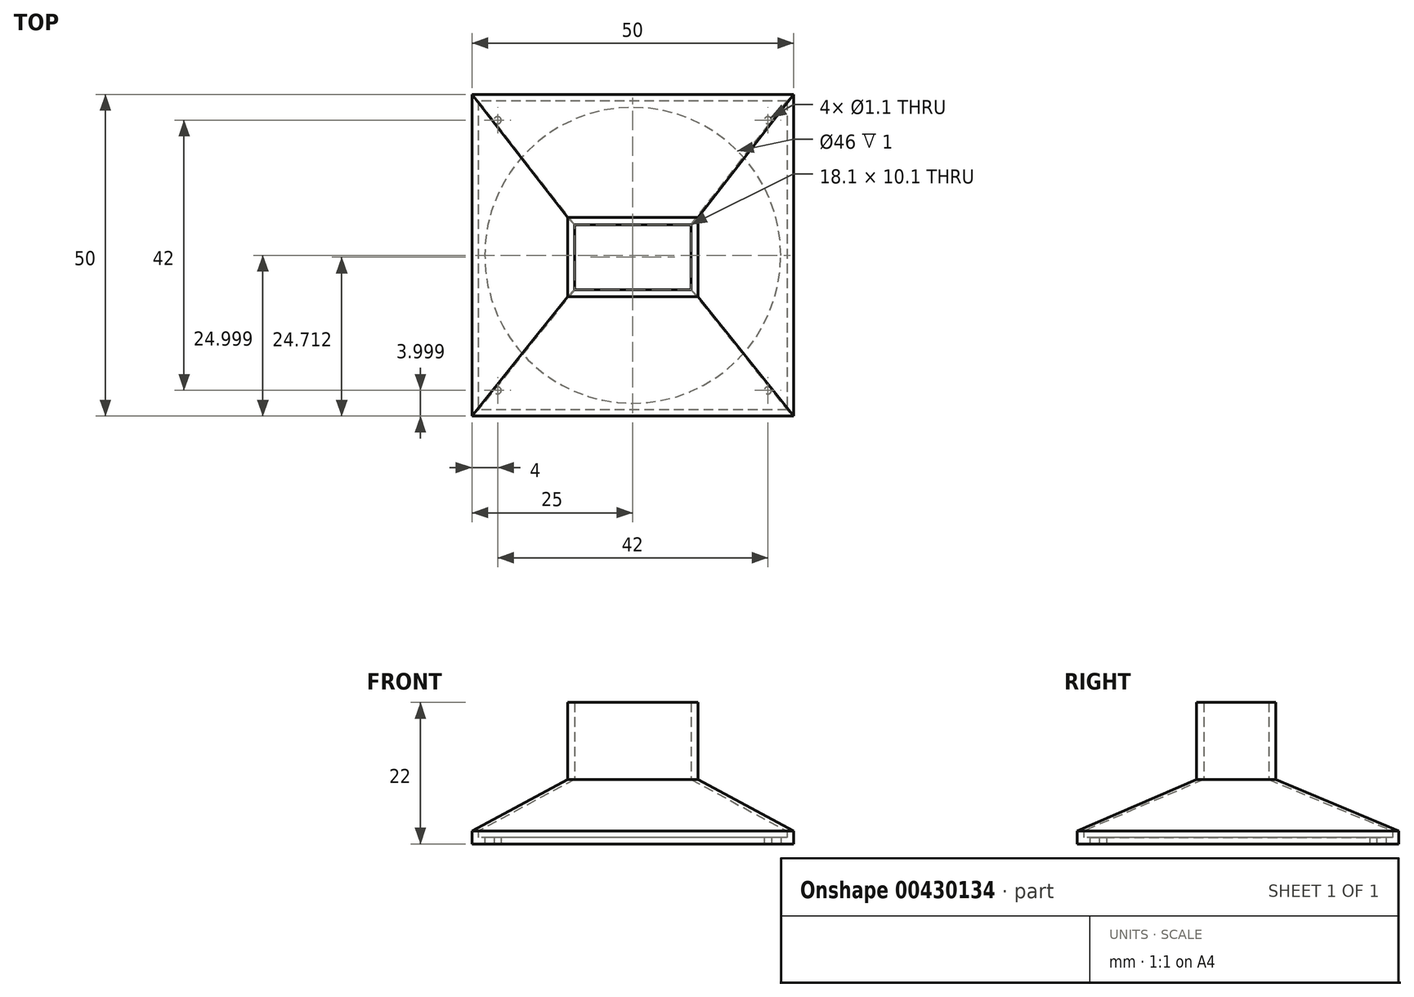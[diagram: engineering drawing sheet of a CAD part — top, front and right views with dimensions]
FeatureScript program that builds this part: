
annotation { "Feature Type Name" : "Feature", "Feature Type Description" : "" }
export const myFeature = defineFeature(function(context is Context, id is Id, definition is map)
    precondition{}
    {
        {
            var Q0;
            Q0=qCreatedBy(makeId("Top.planeOp"),FACE);
            var sketch = newSketch(context, id + "F0", { "sketchPlane" : qUnion([Q0])});
            skPoint(sketch, "E0.middle", {"position": v(0, -0.35) * mm});
            skLineSegment(sketch, "E1", {"start": v(0, 67.46) * mm, "end": v(0, -54.12) * mm, "construction": true});
            skCircle(sketch, "E2", {"center": v(0, -0.35) * mm, "radius": 23 * mm});
            skLineSegment(sketch, "E3.bottom", {"start": v(25, 24.65) * mm, "end": v(-25, 24.65) * mm});
            skLineSegment(sketch, "E3.top", {"start": v(25, -25.35) * mm, "end": v(-25, -25.35) * mm});
            skLineSegment(sketch, "E3.left", {"start": v(25, 24.65) * mm, "end": v(25, -25.35) * mm});
            skLineSegment(sketch, "E3.right", {"start": v(-25, 24.65) * mm, "end": v(-25, -25.35) * mm});
            skCircle(sketch, "E4", {"center": v(21, 20.65) * mm, "radius": 0.55 * mm});
            skCircle(sketch, "E5.MirrorC", {"center": v(-21, 20.65) * mm, "radius": 0.55 * mm});
            skCircle(sketch, "E6.MirrorC", {"center": v(-21, -21.35) * mm, "radius": 0.55 * mm});
            skCircle(sketch, "E7.MirrorC", {"center": v(21, -21.35) * mm, "radius": 0.55 * mm});
            skLineSegment(sketch, "E8.0", {"start": v(24, 23.65) * mm, "end": v(24, -24.35) * mm});
            skLineSegment(sketch, "E8.1", {"start": v(24, 23.65) * mm, "end": v(-24, 23.65) * mm});
            skLineSegment(sketch, "E8.2", {"start": v(-24, 23.65) * mm, "end": v(-24, -24.35) * mm});
            skLineSegment(sketch, "E8.3", {"start": v(24, -24.35) * mm, "end": v(-24, -24.35) * mm});
            skPoint(sketch, "E0.right.end.orphan", {"position": v(-9.05, -5.4) * mm});
            skPoint(sketch, "E9.orphan", {"position": v(-9.05, 4.7) * mm});
            skPoint(sketch, "E0.left.end.orphan", {"position": v(9.05, -5.4) * mm});
            skPoint(sketch, "E0.left.start.orphan", {"position": v(9.05, 4.7) * mm});
            skSolve(sketch);
        }
        {
            var Q0;
            Q0 = qSketchRegion(id + "F0", true);
            extrude(context, id + "F1", {"entities" : qUnion([Q0]), "depth" : 2 * mm});
        }
        {
            var Q0;
            Q0=makeQuery(id+"F0.imprint","IMPRINT",FACE,{"disambiguationData":[TD([[makeQuery(id+"F0.imprint","IMPRINT",EDGE,{"derivedFrom":sQuery(id+"F0.wireOp",EDGE,"E2")}),-1.0]])]});
            extrude(context, id + "F2", {"entities" : qUnion([Q0]), "operationType" : NewBodyOperationType.ADD, "depth" : 1 * mm});
        }
        {
            var Q0;
            Q0=qCreatedBy(makeId("Top.planeOp"),FACE);
            cPlane(context, id + "F3", {"entities" : qUnion([Q0]), "cplaneType" : CPlaneType.OFFSET, "offset" : 10 * mm, "width" : 150 * mm, "height" : 150 * mm});
        }
        {
            var Q0;
            Q0=qCreatedBy(id+"F3.planeOp",FACE);
            var sketch = newSketch(context, id + "F4", { "sketchPlane" : qUnion([Q0])});
            skLineSegment(sketch, "E10.bottom", {"start": v(9.05, 4.41) * mm, "end": v(-9.05, 4.41) * mm});
            skLineSegment(sketch, "E10.top", {"start": v(9.05, -5.69) * mm, "end": v(-9.05, -5.69) * mm});
            skLineSegment(sketch, "E10.left", {"start": v(9.05, 4.41) * mm, "end": v(9.05, -5.69) * mm});
            skLineSegment(sketch, "E10.right", {"start": v(-9.05, 4.41) * mm, "end": v(-9.05, -5.69) * mm});
            skPoint(sketch, "E10.middle", {"position": v(0, -0.64) * mm});
            skLineSegment(sketch, "E11", {"start": v(0, 67.17) * mm, "end": v(0, -54.41) * mm, "construction": true});
            skLineSegment(sketch, "E12.0", {"start": v(-10.15, 5.51) * mm, "end": v(-10.15, -6.79) * mm});
            skLineSegment(sketch, "E12.1", {"start": v(10.15, 5.51) * mm, "end": v(-10.15, 5.51) * mm});
            skLineSegment(sketch, "E12.2", {"start": v(10.15, 5.51) * mm, "end": v(10.15, -6.79) * mm});
            skLineSegment(sketch, "E12.3", {"start": v(10.15, -6.79) * mm, "end": v(-10.15, -6.79) * mm});
            skLineSegment(sketch, "E13", {"start": v(10.15, 5.51) * mm, "end": v(9.05, 4.41) * mm});
            skLineSegment(sketch, "E14", {"start": v(-9.05, 4.41) * mm, "end": v(-10.15, 5.51) * mm});
            skLineSegment(sketch, "E15", {"start": v(10.15, -6.79) * mm, "end": v(9.05, -5.69) * mm});
            skLineSegment(sketch, "E16", {"start": v(-10.15, -6.79) * mm, "end": v(-9.05, -5.69) * mm});
            skSolve(sketch);
        }
        {
            var Q0;
            Q0 = qSketchRegion(id + "F4", true);
            extrude(context, id + "F5", {"entities" : qUnion([Q0]), "depth" : 12 * mm});
        }
        {
            var Q0;
            Q0=makeQuery(id+"F1.opExtrude","CAP_FACE",FACE,{"disambiguationData":[OSD([sQuery(id+"F0.wireOp",EDGE,"E3.bottom"),sQuery(id+"F0.wireOp",EDGE,"E3.top"),sQuery(id+"F0.wireOp",EDGE,"E3.left"),sQuery(id+"F0.wireOp",EDGE,"E3.right"),sQuery(id+"F0.wireOp",EDGE,"E8.0"),sQuery(id+"F0.wireOp",EDGE,"E8.1"),sQuery(id+"F0.wireOp",EDGE,"E8.2"),sQuery(id+"F0.wireOp",EDGE,"E8.3")])],"isStart":false});
            var sketch = newSketch(context, id + "F6", { "sketchPlane" : qUnion([Q0])});
            skLineSegment(sketch, "E17", {"start": v(-24, -24.35) * mm, "end": v(-25, -25.35) * mm});
            skLineSegment(sketch, "E18", {"start": v(-24, 23.65) * mm, "end": v(-25, 24.65) * mm});
            skLineSegment(sketch, "E19", {"start": v(24, 23.65) * mm, "end": v(25, 24.65) * mm});
            skLineSegment(sketch, "E20", {"start": v(25, -25.35) * mm, "end": v(24, -24.35) * mm});
            skSolve(sketch);
        }
        {
            var Q0;
            Q0=makeQuery(id+"F4.imprint","IMPRINT",FACE,{"disambiguationData":[TD([[makeQuery(id+"F4.imprint","IMPRINT",EDGE,{"derivedFrom":sQuery(id+"F4.wireOp",EDGE,"E10.bottom")}),-1.0]])]});
            var Q1;
            Q1=makeQuery(id+"F6.imprint","IMPRINT",FACE,{"disambiguationData":[TD([[makeQuery(id+"F6.imprint","IMPRINT",EDGE,{"derivedFrom":sQuery(id+"F6.wireOp",EDGE,"E18")}),-1.0]])]});
            loft(context, id + "F7", {"sheetProfilesArray" : [{ "sheetProfileEntities" : qUnion([Q0]) }, { "sheetProfileEntities" : qUnion([Q1]) }]});
        }
        {
            var Q0;
            Q0=makeQuery(id+"F6.imprint","IMPRINT",FACE,{"disambiguationData":[TD([[makeQuery(id+"F6.imprint","IMPRINT",EDGE,{"derivedFrom":sQuery(id+"F6.wireOp",EDGE,"E17")}),1.0]])]});
            var Q1;
            Q1=makeQuery(id+"F4.imprint","IMPRINT",FACE,{"disambiguationData":[TD([[makeQuery(id+"F4.imprint","IMPRINT",EDGE,{"derivedFrom":sQuery(id+"F4.wireOp",EDGE,"E10.top")}),1.0]])]});
            loft(context, id + "F8", {"sheetProfilesArray" : [{ "sheetProfileEntities" : qUnion([Q0]) }, { "sheetProfileEntities" : qUnion([Q1]) }]});
        }
        {
            var Q0;
            Q0=makeQuery(id+"F4.imprint","IMPRINT",FACE,{"disambiguationData":[TD([[makeQuery(id+"F4.imprint","IMPRINT",EDGE,{"derivedFrom":sQuery(id+"F4.wireOp",EDGE,"E10.left")}),1.0]])]});
            var Q1;
            Q1=makeQuery(id+"F6.imprint","IMPRINT",FACE,{"disambiguationData":[TD([[makeQuery(id+"F6.imprint","IMPRINT",EDGE,{"derivedFrom":sQuery(id+"F6.wireOp",EDGE,"E19")}),-1.0]])]});
            loft(context, id + "F9", {"sheetProfilesArray" : [{ "sheetProfileEntities" : qUnion([Q0]) }, { "sheetProfileEntities" : qUnion([Q1]) }]});
        }
        {
            var Q0;
            Q0=makeQuery(id+"F4.imprint","IMPRINT",FACE,{"disambiguationData":[TD([[makeQuery(id+"F4.imprint","IMPRINT",EDGE,{"derivedFrom":sQuery(id+"F4.wireOp",EDGE,"E10.right")}),-1.0]])]});
            var Q1;
            Q1=makeQuery(id+"F6.imprint","IMPRINT",FACE,{"disambiguationData":[TD([[makeQuery(id+"F6.imprint","IMPRINT",EDGE,{"derivedFrom":sQuery(id+"F6.wireOp",EDGE,"E17")}),-1.0]])]});
            loft(context, id + "F10", {"sheetProfilesArray" : [{ "sheetProfileEntities" : qUnion([Q0]) }, { "sheetProfileEntities" : qUnion([Q1]) }]});
        }
    });
